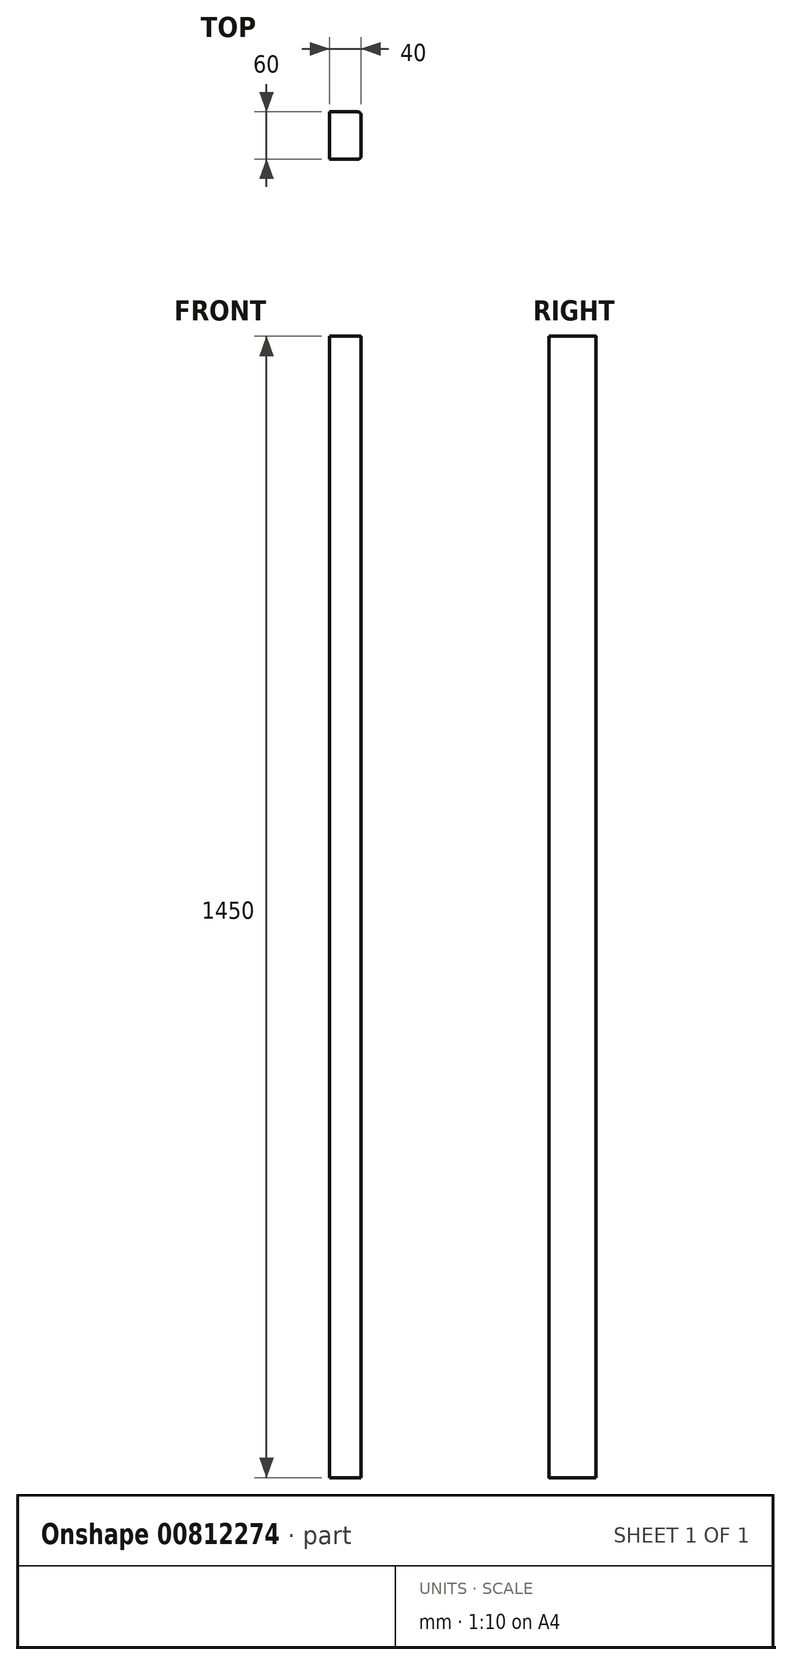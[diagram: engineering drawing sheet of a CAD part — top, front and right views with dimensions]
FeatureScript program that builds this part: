
annotation { "Feature Type Name" : "Feature", "Feature Type Description" : "" }
export const myFeature = defineFeature(function(context is Context, id is Id, definition is map)
    precondition{}
    {
        {
            var Q0;
            Q0=qCreatedBy(makeId("Front.planeOp"),FACE);
            var sketch = newSketch(context, id + "F0", { "sketchPlane" : qUnion([Q0])});
            skLineSegment(sketch, "E0.bottom", {"start": v(20, -725) * mm, "end": v(-20, -725) * mm});
            skLineSegment(sketch, "E0.top", {"start": v(20, 725) * mm, "end": v(-20, 725) * mm});
            skLineSegment(sketch, "E0.left", {"start": v(20, -725) * mm, "end": v(20, 725) * mm});
            skLineSegment(sketch, "E0.right", {"start": v(-20, -725) * mm, "end": v(-20, 725) * mm});
            skPoint(sketch, "E0.middle", {"position": v(0, 0) * mm});
            skSolve(sketch);
        }
        {
            var Q0;
            Q0=makeQuery(id+"F0.imprint","IMPRINT",FACE,{"disambiguationData":[TD([[makeQuery(id+"F0.imprint","IMPRINT",EDGE,{"derivedFrom":sQuery(id+"F0.wireOp",EDGE,"E0.bottom")}),-1.0]])]});
            var Q1;
            Q1=sQuery(id+"F0.wireOp",EDGE,"E0.right");
            extrude(context, id + "F1", {"entities" : qUnion([Q0]), "surfaceEntities" : qUnion([Q1]), "depth" : 60 * mm, "offsetDistance" : 25 * mm});
        }
        {
            var Q0;
            Q0=makeQuery(id+"F1.opExtrude","CAP_EDGE",EDGE,{"disambiguationData":[OSD([sQuery(id+"F0.wireOp",EDGE,"E0.left")])],"isStart":false});
            fillet(context, id + "F2", {"entities" : qUnion([Q0]), "radius" : 4 * mm, "tangentPropagation" : true, "allowEdgeOverflow" : false});
        }
        {
            var Q0;
            Q0=makeQuery(id+"F1.opExtrude","CAP_EDGE",EDGE,{"disambiguationData":[OSD([sQuery(id+"F0.wireOp",EDGE,"E0.left")])],"isStart":true});
            fillet(context, id + "F3", {"entities" : qUnion([Q0]), "radius" : 4 * mm, "tangentPropagation" : true, "allowEdgeOverflow" : false});
        }
    });
